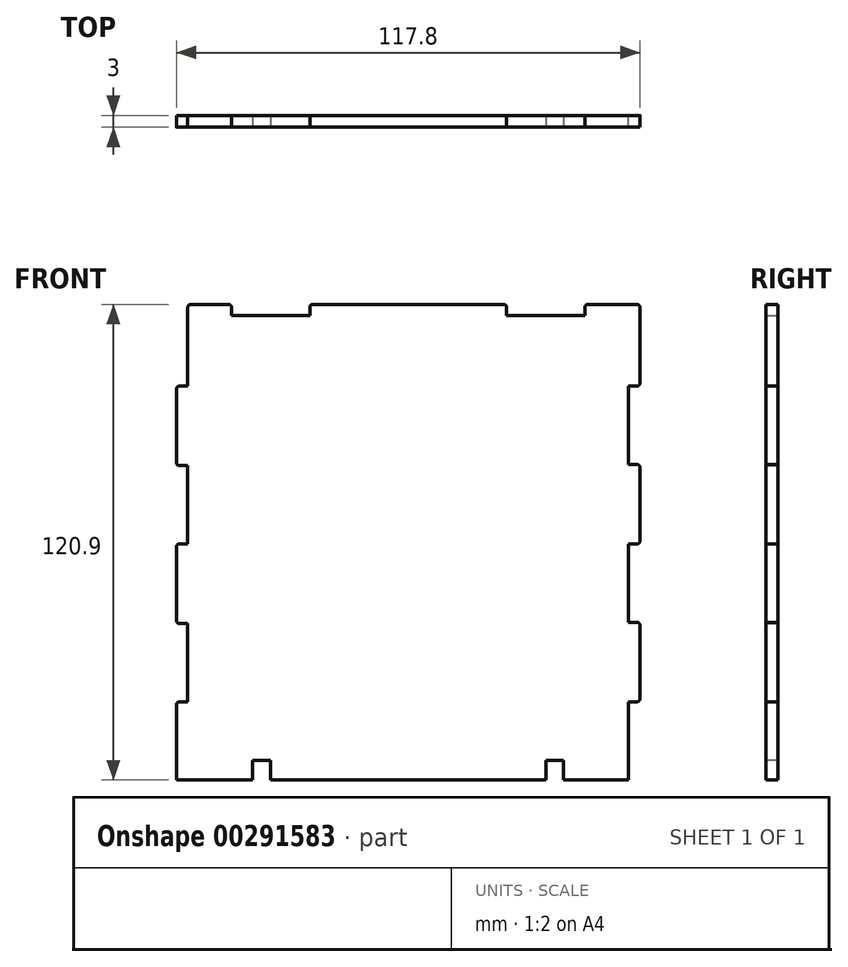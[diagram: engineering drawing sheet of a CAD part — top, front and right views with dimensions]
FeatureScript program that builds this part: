
annotation { "Feature Type Name" : "Feature", "Feature Type Description" : "" }
export const myFeature = defineFeature(function(context is Context, id is Id, definition is map)
    precondition{}
    {
        {
            var Q0;
            Q0=qCreatedBy(makeId("Front.planeOp"),FACE);
            var sketch = newSketch(context, id + "F0", { "sketchPlane" : qUnion([Q0])});
            skLineSegment(sketch, "E0", {"start": v(56, 0) * mm, "end": v(56, 19.9) * mm});
            skLineSegment(sketch, "E1", {"start": v(56, 40.1) * mm, "end": v(56, 60) * mm});
            skLineSegment(sketch, "E2", {"start": v(56, 80.2) * mm, "end": v(56, 100.1) * mm});
            skLineSegment(sketch, "E3", {"start": v(-56, 19.9) * mm, "end": v(-56, 39.8) * mm});
            skLineSegment(sketch, "E4", {"start": v(-56, 60) * mm, "end": v(-56, 79.9) * mm});
            skLineSegment(sketch, "E5", {"start": v(0, 79.55) * mm, "end": v(0, -23.16) * mm, "construction": true});
            skLineSegment(sketch, "E6", {"start": v(56, 19.9) * mm, "end": v(58.9, 19.9) * mm});
            skLineSegment(sketch, "E7", {"start": v(58.9, 19.9) * mm, "end": v(58.9, 40.1) * mm});
            skLineSegment(sketch, "E8", {"start": v(58.9, 40.1) * mm, "end": v(56, 40.1) * mm});
            skLineSegment(sketch, "E9", {"start": v(56, 60) * mm, "end": v(58.9, 60) * mm});
            skLineSegment(sketch, "E10", {"start": v(58.9, 60) * mm, "end": v(58.9, 80.2) * mm});
            skLineSegment(sketch, "E11", {"start": v(58.9, 80.2) * mm, "end": v(56, 80.2) * mm});
            skLineSegment(sketch, "E12", {"start": v(-58.9, 0) * mm, "end": v(-58.9, 19.9) * mm});
            skLineSegment(sketch, "E13", {"start": v(-58.9, 19.9) * mm, "end": v(-56, 19.9) * mm});
            skLineSegment(sketch, "E14", {"start": v(-56, 39.8) * mm, "end": v(-58.9, 39.8) * mm});
            skLineSegment(sketch, "E15", {"start": v(-58.9, 39.8) * mm, "end": v(-58.9, 60) * mm});
            skLineSegment(sketch, "E16", {"start": v(-58.9, 60) * mm, "end": v(-56, 60) * mm});
            skLineSegment(sketch, "E17", {"start": v(-56, 79.9) * mm, "end": v(-58.9, 79.9) * mm});
            skLineSegment(sketch, "E18", {"start": v(-58.9, 79.9) * mm, "end": v(-58.9, 100.1) * mm});
            skLineSegment(sketch, "E19", {"start": v(-58.9, 100.1) * mm, "end": v(-56, 100.1) * mm});
            skLineSegment(sketch, "E20", {"start": v(-110.96, 118) * mm, "end": v(104.76, 118) * mm, "construction": true});
            skLineSegment(sketch, "E21", {"start": v(-58.9, 0) * mm, "end": v(56, 0) * mm});
            skLineSegment(sketch, "E22", {"start": v(-110.96, 120.9) * mm, "end": v(104.76, 120.9) * mm, "construction": true});
            skLineSegment(sketch, "E23", {"start": v(-56, 100.1) * mm, "end": v(-56, 120.9) * mm});
            skLineSegment(sketch, "E24", {"start": v(56, 100.1) * mm, "end": v(58.9, 100.1) * mm});
            skLineSegment(sketch, "E25", {"start": v(58.9, 100.1) * mm, "end": v(58.9, 120.9) * mm});
            skLineSegment(sketch, "E26", {"start": v(-56, 120.9) * mm, "end": v(-44.9, 120.9) * mm});
            skLineSegment(sketch, "E27", {"start": v(-44.9, 120.9) * mm, "end": v(-44.9, 118) * mm});
            skLineSegment(sketch, "E28", {"start": v(-44.9, 118) * mm, "end": v(-25, 118) * mm});
            skLineSegment(sketch, "E29", {"start": v(-25, 118) * mm, "end": v(-25, 120.9) * mm});
            skLineSegment(sketch, "E30", {"start": v(-25, 120.9) * mm, "end": v(25, 120.9) * mm});
            skLineSegment(sketch, "E31", {"start": v(25, 120.9) * mm, "end": v(25, 118) * mm});
            skLineSegment(sketch, "E32", {"start": v(25, 118) * mm, "end": v(44.9, 118) * mm});
            skLineSegment(sketch, "E33", {"start": v(44.9, 118) * mm, "end": v(44.9, 120.9) * mm});
            skLineSegment(sketch, "E34", {"start": v(44.9, 120.9) * mm, "end": v(58.9, 120.9) * mm});
            skSolve(sketch);
        }
        {
            var Q0;
            Q0=makeQuery(id+"F0.imprint","IMPRINT",FACE,{"disambiguationData":[TD([[makeQuery(id+"F0.imprint","IMPRINT",EDGE,{"derivedFrom":sQuery(id+"F0.wireOp",EDGE,"E0")}),1.0]])]});
            extrude(context, id + "F1", {"entities" : qUnion([Q0]), "depth" : 3 * mm});
        }
        {
            var Q0;
            Q0=makeQuery(id+"F1.opExtrude","SWEPT_EDGE",EDGE,{"disambiguationData":[OSD([sQuery(id+"F0.wireOp",EDGE,"E24"),sQuery(id+"F0.wireOp",EDGE,"E25")])]});
            var Q1;
            Q1=makeQuery(id+"F1.opExtrude","SWEPT_EDGE",EDGE,{"disambiguationData":[OSD([sQuery(id+"F0.wireOp",EDGE,"E10"),sQuery(id+"F0.wireOp",EDGE,"E11")])]});
            var Q2;
            Q2=makeQuery(id+"F1.opExtrude","SWEPT_EDGE",EDGE,{"disambiguationData":[OSD([sQuery(id+"F0.wireOp",EDGE,"E9"),sQuery(id+"F0.wireOp",EDGE,"E10")])]});
            var Q3;
            Q3=makeQuery(id+"F1.opExtrude","SWEPT_EDGE",EDGE,{"disambiguationData":[OSD([sQuery(id+"F0.wireOp",EDGE,"E7"),sQuery(id+"F0.wireOp",EDGE,"E8")])]});
            var Q4;
            Q4=makeQuery(id+"F1.opExtrude","SWEPT_EDGE",EDGE,{"disambiguationData":[OSD([sQuery(id+"F0.wireOp",EDGE,"E6"),sQuery(id+"F0.wireOp",EDGE,"E7")])]});
            var Q5;
            Q5=makeQuery(id+"F1.opExtrude","SWEPT_EDGE",EDGE,{"disambiguationData":[OSD([sQuery(id+"F0.wireOp",EDGE,"E12"),sQuery(id+"F0.wireOp",EDGE,"E13")])]});
            var Q6;
            Q6=makeQuery(id+"F1.opExtrude","SWEPT_EDGE",EDGE,{"disambiguationData":[OSD([sQuery(id+"F0.wireOp",EDGE,"E14"),sQuery(id+"F0.wireOp",EDGE,"E15")])]});
            var Q7;
            Q7=makeQuery(id+"F1.opExtrude","SWEPT_EDGE",EDGE,{"disambiguationData":[OSD([sQuery(id+"F0.wireOp",EDGE,"E15"),sQuery(id+"F0.wireOp",EDGE,"E16")])]});
            var Q8;
            Q8=makeQuery(id+"F1.opExtrude","SWEPT_EDGE",EDGE,{"disambiguationData":[OSD([sQuery(id+"F0.wireOp",EDGE,"E17"),sQuery(id+"F0.wireOp",EDGE,"E18")])]});
            var Q9;
            Q9=makeQuery(id+"F1.opExtrude","SWEPT_EDGE",EDGE,{"disambiguationData":[OSD([sQuery(id+"F0.wireOp",EDGE,"E18"),sQuery(id+"F0.wireOp",EDGE,"E19")])]});
            var Q10;
            Q10=makeQuery(id+"F1.opExtrude","SWEPT_EDGE",EDGE,{"disambiguationData":[OSD([sQuery(id+"F0.wireOp",EDGE,"E23"),sQuery(id+"F0.wireOp",EDGE,"E26")])]});
            var Q11;
            Q11=makeQuery(id+"F1.opExtrude","SWEPT_EDGE",EDGE,{"disambiguationData":[OSD([sQuery(id+"F0.wireOp",EDGE,"E26"),sQuery(id+"F0.wireOp",EDGE,"E27")])]});
            var Q12;
            Q12=makeQuery(id+"F1.opExtrude","SWEPT_EDGE",EDGE,{"disambiguationData":[OSD([sQuery(id+"F0.wireOp",EDGE,"E29"),sQuery(id+"F0.wireOp",EDGE,"E30")])]});
            var Q13;
            Q13=makeQuery(id+"F1.opExtrude","SWEPT_EDGE",EDGE,{"disambiguationData":[OSD([sQuery(id+"F0.wireOp",EDGE,"E30"),sQuery(id+"F0.wireOp",EDGE,"E31")])]});
            var Q14;
            Q14=makeQuery(id+"F1.opExtrude","SWEPT_EDGE",EDGE,{"disambiguationData":[OSD([sQuery(id+"F0.wireOp",EDGE,"E33"),sQuery(id+"F0.wireOp",EDGE,"E34")])]});
            var Q15;
            Q15=makeQuery(id+"F1.opExtrude","SWEPT_EDGE",EDGE,{"disambiguationData":[OSD([sQuery(id+"F0.wireOp",EDGE,"E25"),sQuery(id+"F0.wireOp",EDGE,"E34")])]});
            fillet(context, id + "F2", {"entities" : qUnion([Q0, Q1, Q2, Q3, Q4, Q5, Q6, Q7, Q8, Q9, Q10, Q11, Q12, Q13, Q14, Q15]), "radius" : .8 * mm, "tangentPropagation" : true, "allowEdgeOverflow" : false});
        }
        {
            var Q0;
            Q0=makeQuery(id+"F1.opExtrude","CAP_FACE",FACE,{"disambiguationData":[OSD([sQuery(id+"F0.wireOp",EDGE,"E0"),sQuery(id+"F0.wireOp",EDGE,"E1"),sQuery(id+"F0.wireOp",EDGE,"E2"),sQuery(id+"F0.wireOp",EDGE,"E3"),sQuery(id+"F0.wireOp",EDGE,"E4"),sQuery(id+"F0.wireOp",EDGE,"E6"),sQuery(id+"F0.wireOp",EDGE,"E7"),sQuery(id+"F0.wireOp",EDGE,"E8"),sQuery(id+"F0.wireOp",EDGE,"E9"),sQuery(id+"F0.wireOp",EDGE,"E10"),sQuery(id+"F0.wireOp",EDGE,"E11"),sQuery(id+"F0.wireOp",EDGE,"E12"),sQuery(id+"F0.wireOp",EDGE,"E13"),sQuery(id+"F0.wireOp",EDGE,"E14"),sQuery(id+"F0.wireOp",EDGE,"E15"),sQuery(id+"F0.wireOp",EDGE,"E16"),sQuery(id+"F0.wireOp",EDGE,"E17"),sQuery(id+"F0.wireOp",EDGE,"E18"),sQuery(id+"F0.wireOp",EDGE,"E19"),sQuery(id+"F0.wireOp",EDGE,"E21"),sQuery(id+"F0.wireOp",EDGE,"E23"),sQuery(id+"F0.wireOp",EDGE,"E24"),sQuery(id+"F0.wireOp",EDGE,"E25"),sQuery(id+"F0.wireOp",EDGE,"E26"),sQuery(id+"F0.wireOp",EDGE,"E27"),sQuery(id+"F0.wireOp",EDGE,"E28"),sQuery(id+"F0.wireOp",EDGE,"E29"),sQuery(id+"F0.wireOp",EDGE,"E30"),sQuery(id+"F0.wireOp",EDGE,"E31"),sQuery(id+"F0.wireOp",EDGE,"E32"),sQuery(id+"F0.wireOp",EDGE,"E33"),sQuery(id+"F0.wireOp",EDGE,"E34")])],"isStart":false});
            var sketch = newSketch(context, id + "F3", { "sketchPlane" : qUnion([Q0])});
            skLineSegment(sketch, "E35", {"start": v(-39.5, 0) * mm, "end": v(-39.5, 5) * mm});
            skLineSegment(sketch, "E36", {"start": v(-39.5, 5) * mm, "end": v(-35, 5) * mm});
            skLineSegment(sketch, "E37", {"start": v(-35, 5) * mm, "end": v(-35, 0) * mm});
            skLineSegment(sketch, "E38", {"start": v(-35, 0) * mm, "end": v(-39.5, 0) * mm});
            skLineSegment(sketch, "E39", {"start": v(35, 0) * mm, "end": v(35, 5) * mm});
            skLineSegment(sketch, "E40", {"start": v(35, 5) * mm, "end": v(39.5, 5) * mm});
            skLineSegment(sketch, "E41", {"start": v(39.5, 5) * mm, "end": v(39.5, 0) * mm});
            skLineSegment(sketch, "E42", {"start": v(39.5, 0) * mm, "end": v(35, 0) * mm});
            skSolve(sketch);
        }
        {
            var Q0;
            Q0=makeQuery(id+"F3.imprint","IMPRINT",FACE,{"disambiguationData":[TD([[makeQuery(id+"F3.imprint","IMPRINT",EDGE,{"derivedFrom":sQuery(id+"F3.wireOp",EDGE,"E35")}),-1.0]])]});
            var Q1;
            Q1=makeQuery(id+"F3.imprint","IMPRINT",FACE,{"disambiguationData":[TD([[makeQuery(id+"F3.imprint","IMPRINT",EDGE,{"derivedFrom":sQuery(id+"F3.wireOp",EDGE,"E39")}),-1.0]])]});
            extrude(context, id + "F4", {"entities" : qUnion([Q0, Q1]), "operationType" : NewBodyOperationType.REMOVE, "endBound" : BoundingType.THROUGH_ALL, "oppositeDirection" : true, "depth" : 25 * mm});
        }
    });
